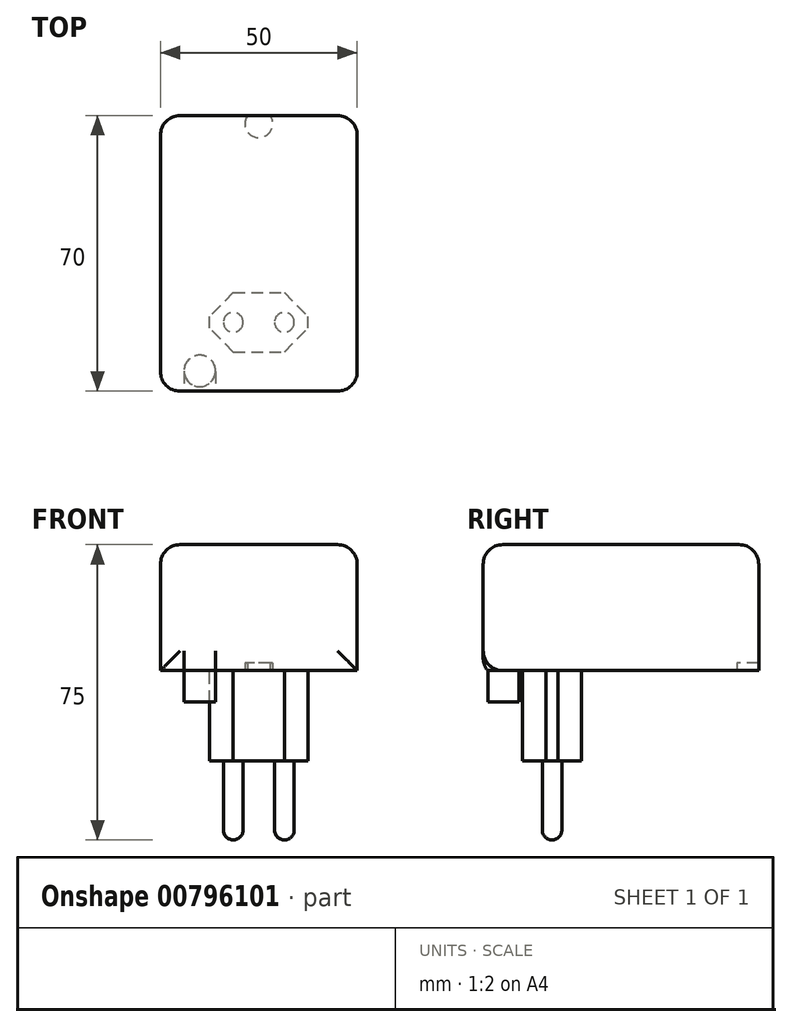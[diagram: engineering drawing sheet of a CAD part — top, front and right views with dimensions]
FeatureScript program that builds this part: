
annotation { "Feature Type Name" : "Feature", "Feature Type Description" : "" }
export const myFeature = defineFeature(function(context is Context, id is Id, definition is map)
    precondition{}
    {
        {
            var Q0;
            Q0=qCreatedBy(makeId("Top.planeOp"),FACE);
            var sketch = newSketch(context, id + "F0", { "sketchPlane" : qUnion([Q0])});
            skLineSegment(sketch, "E0.bottom", {"start": v(25, -35) * mm, "end": v(-25, -35) * mm});
            skLineSegment(sketch, "E0.top", {"start": v(25, 35) * mm, "end": v(-25, 35) * mm});
            skLineSegment(sketch, "E0.left", {"start": v(25, -35) * mm, "end": v(25, 35) * mm});
            skLineSegment(sketch, "E0.right", {"start": v(-25, -35) * mm, "end": v(-25, 35) * mm});
            skPoint(sketch, "E0.middle", {"position": v(0, 0) * mm});
            skSolve(sketch);
        }
        {
            var Q0;
            Q0 = qSketchRegion(id + "F0", true);
            extrude(context, id + "F1", {"entities" : qUnion([Q0]), "depth" : 40 * mm, "offsetDistance" : 25 * mm});
        }
        {
            var Q0;
            Q0=makeQuery(id+"F1.opExtrude","CAP_FACE",FACE,{"disambiguationData":[OSD([sQuery(id+"F0.wireOp",EDGE,"E0.bottom"),sQuery(id+"F0.wireOp",EDGE,"E0.top"),sQuery(id+"F0.wireOp",EDGE,"E0.left"),sQuery(id+"F0.wireOp",EDGE,"E0.right")])],"isStart":true});
            var sketch = newSketch(context, id + "F2", { "sketchPlane" : qUnion([Q0])});
            skLineSegment(sketch, "E1", {"start": v(-25, 20) * mm, "end": v(-12.5, 20) * mm});
            skLineSegment(sketch, "E2", {"start": v(-25, -35) * mm, "end": v(-25, 20) * mm});
            skPoint(sketch, "E3.middle", {"position": v(-12.5, 20) * mm});
            skLineSegment(sketch, "E4", {"start": v(25, 35) * mm, "end": v(25, 25) * mm});
            skLineSegment(sketch, "E5", {"start": v(-12.5, 25) * mm, "end": v(-12.5, 35) * mm});
            skPoint(sketch, "E6.middle", {"position": v(-12.5, 25) * mm});
            skLineSegment(sketch, "E7.bottom", {"start": v(-12.5, 25) * mm, "end": v(12.5, 25) * mm});
            skLineSegment(sketch, "E7.top", {"start": v(-12.5, 10) * mm, "end": v(12.5, 10) * mm});
            skLineSegment(sketch, "E7.left", {"start": v(-12.5, 25) * mm, "end": v(-12.5, 10) * mm});
            skLineSegment(sketch, "E7.right", {"start": v(12.5, 25) * mm, "end": v(12.5, 17.5) * mm});
            skLineSegment(sketch, "E8.cCircle", {"start": v(12.5, 17.5) * mm, "end": v(12.5, 17.5) * mm});
            skPoint(sketch, "E8.0.midPoint", {"position": v(12.5, 17.5) * mm});
            skPoint(sketch, "E9.orphan", {"position": v(0, 27.8) * mm});
            skLineSegment(sketch, "E10.trimOffspring", {"start": v(12.5, 17.5) * mm, "end": v(12.5, 10) * mm});
            skSolve(sketch);
        }
        {
            var Q0;
            {var subQ3=sQuery(id+"F2.wireOp",EDGE,"E7.bottom");Q0=makeQuery(id+"F2.imprint","IMPRINT",FACE,{"disambiguationData":[TD([[makeQuery(id+"F2.imprint","IMPRINT",EDGE,{"derivedFrom":subQ3}),-1.0]])]});}
            extrude(context, id + "F3", {"entities" : qUnion([Q0]), "operationType" : NewBodyOperationType.ADD, "depth" : 15 * mm, "offsetDistance" : 25 * mm});
        }
        {
            var Q0;
            Q0=makeQuery(id+"F3.opExtrude","SWEPT_EDGE",EDGE,{"disambiguationData":[OSD([sQuery(id+"F2.wireOp",EDGE,"E5"),sQuery(id+"F2.wireOp",EDGE,"E7.bottom"),sQuery(id+"F2.wireOp",EDGE,"E7.left")])]});
            var Q1;
            Q1=makeQuery(id+"F3.opExtrude","SWEPT_EDGE",EDGE,{"disambiguationData":[OSD([sQuery(id+"F2.wireOp",EDGE,"E7.top"),sQuery(id+"F2.wireOp",EDGE,"E7.left")])]});
            var Q2;
            Q2=makeQuery(id+"F3.opExtrude","SWEPT_EDGE",EDGE,{"disambiguationData":[OSD([sQuery(id+"F2.wireOp",EDGE,"E7.top"),sQuery(id+"F2.wireOp",EDGE,"E10.trimOffspring")])]});
            var Q3;
            Q3=makeQuery(id+"F3.opExtrude","SWEPT_EDGE",EDGE,{"disambiguationData":[OSD([sQuery(id+"F2.wireOp",EDGE,"E7.bottom"),sQuery(id+"F2.wireOp",EDGE,"E7.right")])]});
            chamfer(context, id + "F4", {"entities" : qUnion([Q0, Q1, Q2, Q3]), "width" : 6 * mm, "tangentPropagation" : true});
        }
        {
            var Q0;
            Q0=makeQuery(id+"F3.opExtrude","CAP_FACE",FACE,{"disambiguationData":[OSD([sQuery(id+"F2.wireOp",EDGE,"E7.bottom"),sQuery(id+"F2.wireOp",EDGE,"E7.top"),sQuery(id+"F2.wireOp",EDGE,"E7.left"),sQuery(id+"F2.wireOp",EDGE,"E7.right"),sQuery(id+"F2.wireOp",EDGE,"E10.trimOffspring")])],"isStart":false});
            var sketch = newSketch(context, id + "F5", { "sketchPlane" : qUnion([Q0])});
            skLineSegment(sketch, "E11", {"start": v(-6.5, 25) * mm, "end": v(-6.5, 17.5) * mm});
            skLineSegment(sketch, "E12", {"start": v(6.5, 25) * mm, "end": v(6.5, 17.5) * mm});
            skCircle(sketch, "E13", {"center": v(-6.5, 17.5) * mm, "radius": 2.5 * mm});
            skCircle(sketch, "E14", {"center": v(6.5, 17.5) * mm, "radius": 2.5 * mm});
            skSolve(sketch);
        }
        {
            var Q0;
            Q0=makeQuery(id+"F5.imprint","IMPRINT",FACE,{"disambiguationData":[TD([[makeQuery(id+"F5.imprint","IMPRINT",EDGE,{"derivedFrom":sQuery(id+"F5.wireOp",EDGE,"E13")}),1.0]])]});
            extrude(context, id + "F6", {"entities" : qUnion([Q0]), "operationType" : NewBodyOperationType.ADD, "depth" : 20 * mm, "offsetDistance" : 25 * mm});
        }
        {
            var Q0;
            Q0=makeQuery(id+"F5.imprint","IMPRINT",FACE,{"disambiguationData":[TD([[makeQuery(id+"F5.imprint","IMPRINT",EDGE,{"derivedFrom":sQuery(id+"F5.wireOp",EDGE,"E14")}),1.0]])]});
            extrude(context, id + "F7", {"entities" : qUnion([Q0]), "operationType" : NewBodyOperationType.ADD, "depth" : 20 * mm, "offsetDistance" : 25 * mm});
        }
        {
            var Q0;
            Q0=makeQuery(id+"F6.opExtrude","CAP_FACE",FACE,{"disambiguationData":[OSD([sQuery(id+"F5.wireOp",EDGE,"E13")])],"isStart":false});
            var Q1;
            Q1=makeQuery(id+"F7.opExtrude","CAP_FACE",FACE,{"disambiguationData":[OSD([sQuery(id+"F5.wireOp",EDGE,"E14")])],"isStart":false});
            fillet(context, id + "F8", {"entities" : qUnion([Q0, Q1]), "radius" : 2.5 * mm, "tangentPropagation" : true, "allowEdgeOverflow" : false});
        }
        {
            var Q0;
            Q0=makeQuery(id+"F1.opExtrude","CAP_FACE",FACE,{"disambiguationData":[OSD([sQuery(id+"F0.wireOp",EDGE,"E0.bottom"),sQuery(id+"F0.wireOp",EDGE,"E0.top"),sQuery(id+"F0.wireOp",EDGE,"E0.left"),sQuery(id+"F0.wireOp",EDGE,"E0.right")])],"isStart":true});
            var sketch = newSketch(context, id + "F9", { "sketchPlane" : qUnion([Q0])});
            skArc(sketch, "E15", {"start": v(2.87, -35) * mm, "mid": v(0, -29.42) * mm, "end": v(-2.87, -35) * mm});
            skLineSegment(sketch, "E16", {"start": v(-2.87, -35) * mm, "end": v(2.87, -35) * mm});
            skSolve(sketch);
        }
        {
            var Q0;
            Q0 = qSketchRegion(id + "F9", true);
            extrude(context, id + "F10", {"entities" : qUnion([Q0]), "operationType" : NewBodyOperationType.REMOVE, "oppositeDirection" : true, "depth" : 10 * mm, "offsetDistance" : 25 * mm});
        }
        {
            var Q0;
            Q0=makeQuery(id+"F1.opExtrude","CAP_FACE",FACE,{"disambiguationData":[OSD([sQuery(id+"F0.wireOp",EDGE,"E0.bottom"),sQuery(id+"F0.wireOp",EDGE,"E0.top"),sQuery(id+"F0.wireOp",EDGE,"E0.left"),sQuery(id+"F0.wireOp",EDGE,"E0.right")])],"isStart":true});
            var sketch = newSketch(context, id + "F11", { "sketchPlane" : qUnion([Q0])});
            skCircle(sketch, "E17", {"center": v(15, 29.84) * mm, "radius": 4 * mm});
            skLineSegment(sketch, "E18", {"start": v(15, 29.84) * mm, "end": v(-28.94, 29.84) * mm});
            skLineSegment(sketch, "E19", {"start": v(25, 29.84) * mm, "end": v(15, 29.84) * mm});
            skLineSegment(sketch, "E20", {"start": v(-25, 29.84) * mm, "end": v(-15, 29.84) * mm});
            skCircle(sketch, "E21", {"center": v(-15, 29.84) * mm, "radius": 4 * mm});
            skSolve(sketch);
        }
        {
            var Q0;
            {var subQ0=sQuery(id+"F11.wireOp",EDGE,"E18");var subQ1=sQuery(id+"F11.wireOp",EDGE,"E17");var subQ2=makeQuery(id+"F11.imprint","INTERSECT",VERTEX,{"derivedFrom":[subQ1,subQ0]});Q0=makeQuery(id+"F11.imprint","IMPRINT",FACE,{"disambiguationData":[TD([[makeQuery(id+"F11.imprint","IMPRINT",EDGE,{"disambiguationData":[TD([[subQ2,-1.0]])],"derivedFrom":subQ1}),1.0]])]});}
            var Q1;
            {var subQ0=sQuery(id+"F11.wireOp",EDGE,"E20");var subQ1=sQuery(id+"F11.wireOp",EDGE,"E18");var subQ2=makeQuery(id+"F11.imprint","INTERSECT",VERTEX,{"derivedFrom":[subQ1,subQ0]});Q1=makeQuery(id+"F11.imprint","IMPRINT",FACE,{"disambiguationData":[TD([[makeQuery(id+"F11.imprint","IMPRINT",EDGE,{"disambiguationData":[TD([[subQ2,1.0]])],"derivedFrom":subQ1}),-1.0]])]});}
            var Q2;
            {var subQ0=sQuery(id+"F11.wireOp",EDGE,"E20");var subQ1=sQuery(id+"F11.wireOp",EDGE,"E18");var subQ2=makeQuery(id+"F11.imprint","INTERSECT",VERTEX,{"derivedFrom":[subQ1,subQ0]});Q2=makeQuery(id+"F11.imprint","IMPRINT",FACE,{"disambiguationData":[TD([[makeQuery(id+"F11.imprint","IMPRINT",EDGE,{"disambiguationData":[TD([[subQ2,1.0]])],"derivedFrom":subQ1}),1.0]])]});}
            var Q3;
            {var subQ0=sQuery(id+"F11.wireOp",EDGE,"E18");var subQ1=sQuery(id+"F11.wireOp",EDGE,"E17");var subQ2=makeQuery(id+"F11.imprint","INTERSECT",VERTEX,{"derivedFrom":[subQ1,subQ0]});Q3=makeQuery(id+"F11.imprint","IMPRINT",FACE,{"disambiguationData":[TD([[makeQuery(id+"F11.imprint","IMPRINT",EDGE,{"disambiguationData":[TD([[subQ2,1.0]])],"derivedFrom":subQ1}),1.0]])]});}
            extrude(context, id + "F12", {"entities" : qUnion([Q0, Q1, Q2, Q3]), "operationType" : NewBodyOperationType.REMOVE, "oppositeDirection" : true, "depth" : 8 * mm, "offsetDistance" : 25 * mm});
        }
        {
            var Q0;
            Q0=makeQuery(id+"F1.opExtrude","CAP_EDGE",EDGE,{"disambiguationData":[OSD([sQuery(id+"F0.wireOp",EDGE,"E0.left")])],"isStart":true});
            var Q1;
            Q1=makeQuery(id+"F1.opExtrude","SWEPT_EDGE",EDGE,{"disambiguationData":[OSD([sQuery(id+"F0.wireOp",EDGE,"E0.bottom"),sQuery(id+"F0.wireOp",EDGE,"E0.left")])]});
            var Q2;
            Q2=makeQuery(id+"F1.opExtrude","CAP_EDGE",EDGE,{"disambiguationData":[OSD([sQuery(id+"F0.wireOp",EDGE,"E0.left")])],"isStart":false});
            var Q3;
            Q3=makeQuery(id+"F1.opExtrude","SWEPT_EDGE",EDGE,{"disambiguationData":[OSD([sQuery(id+"F0.wireOp",EDGE,"E0.top"),sQuery(id+"F0.wireOp",EDGE,"E0.left")])]});
            var Q4;
            {var subQ0=sQuery(id+"F0.wireOp",EDGE,"E0.left");var subQ1=sQuery(id+"F0.wireOp",EDGE,"E0.top");Q4=makeQuery(id+"F10.boolean.opBoolean","SPLIT",EDGE,{"disambiguationData":[TD([makeQuery(id+"F1.opExtrude","SWEPT_FACE",FACE,{"disambiguationData":[OSD([subQ0])]})])],"derivedFrom":makeQuery(id+"F1.opExtrude","CAP_EDGE",EDGE,{"disambiguationData":[OSD([subQ1])],"isStart":true})});}
            var Q5;
            {var subQ0=sQuery(id+"F0.wireOp",EDGE,"E0.right");var subQ1=sQuery(id+"F0.wireOp",EDGE,"E0.top");Q5=makeQuery(id+"F10.boolean.opBoolean","SPLIT",EDGE,{"disambiguationData":[TD([makeQuery(id+"F1.opExtrude","SWEPT_FACE",FACE,{"disambiguationData":[OSD([subQ0])]})])],"derivedFrom":makeQuery(id+"F1.opExtrude","CAP_EDGE",EDGE,{"disambiguationData":[OSD([subQ1])],"isStart":true})});}
            var Q6;
            Q6=makeQuery(id+"F1.opExtrude","CAP_EDGE",EDGE,{"disambiguationData":[OSD([sQuery(id+"F0.wireOp",EDGE,"E0.right")])],"isStart":true});
            var Q7;
            Q7=makeQuery(id+"F1.opExtrude","SWEPT_EDGE",EDGE,{"disambiguationData":[OSD([sQuery(id+"F0.wireOp",EDGE,"E0.bottom"),sQuery(id+"F0.wireOp",EDGE,"E0.right")])]});
            var Q8;
            Q8=makeQuery(id+"F1.opExtrude","SWEPT_EDGE",EDGE,{"disambiguationData":[OSD([sQuery(id+"F0.wireOp",EDGE,"E0.top"),sQuery(id+"F0.wireOp",EDGE,"E0.right")])]});
            var Q9;
            Q9=makeQuery(id+"F1.opExtrude","SWEPT_FACE",FACE,{"disambiguationData":[OSD([sQuery(id+"F0.wireOp",EDGE,"E0.bottom")])]});
            var Q10;
            Q10=makeQuery(id+"F1.opExtrude","CAP_EDGE",EDGE,{"disambiguationData":[OSD([sQuery(id+"F0.wireOp",EDGE,"E0.right")])],"isStart":false});
            var Q11;
            Q11=makeQuery(id+"F1.opExtrude","CAP_EDGE",EDGE,{"disambiguationData":[OSD([sQuery(id+"F0.wireOp",EDGE,"E0.top")])],"isStart":false});
            fillet(context, id + "F13", {"entities" : qUnion([Q0, Q1, Q2, Q3, Q4, Q5, Q6, Q7, Q8, Q9, Q10, Q11]), "radius" : 5 * mm, "tangentPropagation" : true, "allowEdgeOverflow" : false});
        }
    });
